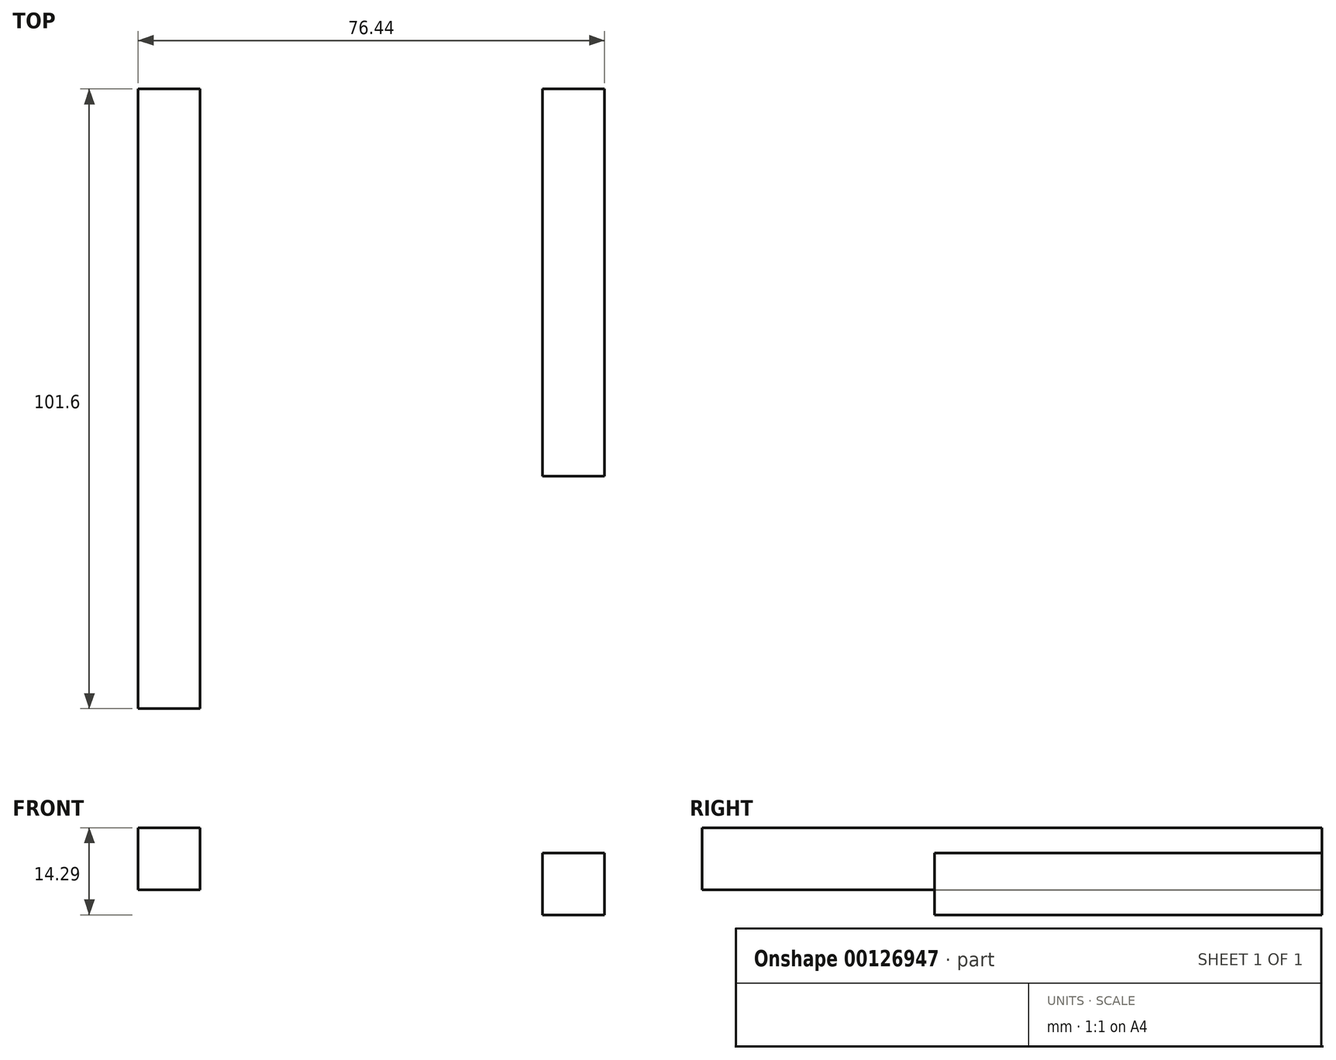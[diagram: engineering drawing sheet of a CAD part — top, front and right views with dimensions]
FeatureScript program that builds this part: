
annotation { "Feature Type Name" : "Feature", "Feature Type Description" : "" }
export const myFeature = defineFeature(function(context is Context, id is Id, definition is map)
    precondition{}
    {
        {
            var Q0;
            Q0=qCreatedBy(makeId("Front.planeOp"),FACE);
            var sketch = newSketch(context, id + "F0", { "sketchPlane" : qUnion([Q0])});
            skLineSegment(sketch, "E0.bottom", {"start": v(-36.86, 23.53) * mm, "end": v(-47.02, 23.53) * mm});
            skLineSegment(sketch, "E0.top", {"start": v(-36.86, 33.69) * mm, "end": v(-47.02, 33.69) * mm});
            skLineSegment(sketch, "E0.left", {"start": v(-36.86, 23.53) * mm, "end": v(-36.86, 33.69) * mm});
            skLineSegment(sketch, "E0.right", {"start": v(-47.02, 23.53) * mm, "end": v(-47.02, 33.69) * mm});
            skPoint(sketch, "E0.middle", {"position": v(-41.94, 28.6) * mm});
            skSolve(sketch);
        }
        {
            var Q0;
            Q0=makeQuery(id+"F0.imprint","IMPRINT",FACE,{"disambiguationData":[TD([[makeQuery(id+"F0.imprint","IMPRINT",EDGE,{"derivedFrom":sQuery(id+"F0.wireOp",EDGE,"E0.bottom")}),-1.0]])]});
            extrude(context, id + "F1", {"entities" : qUnion([Q0]), "depth" : 101.6 * mm});
        }
        {
            var Q0;
            Q0=qCreatedBy(makeId("Front.planeOp"),FACE);
            var sketch = newSketch(context, id + "F2", { "sketchPlane" : qUnion([Q0])});
            skLineSegment(sketch, "E1.bottom", {"start": v(19.26, 29.56) * mm, "end": v(29.42, 29.56) * mm});
            skLineSegment(sketch, "E1.top", {"start": v(19.26, 19.4) * mm, "end": v(29.42, 19.4) * mm});
            skLineSegment(sketch, "E1.left", {"start": v(19.26, 29.56) * mm, "end": v(19.26, 19.4) * mm});
            skLineSegment(sketch, "E1.right", {"start": v(29.42, 29.56) * mm, "end": v(29.42, 19.4) * mm});
            skSolve(sketch);
        }
        {
            var Q0;
            Q0=makeQuery(id+"F2.imprint","IMPRINT",FACE,{"disambiguationData":[TD([[makeQuery(id+"F2.imprint","IMPRINT",EDGE,{"derivedFrom":sQuery(id+"F2.wireOp",EDGE,"E1.bottom")}),-1.0]])]});
            extrude(context, id + "F3", {"entities" : qUnion([Q0]), "depth" : 63.5 * mm});
        }
    });
